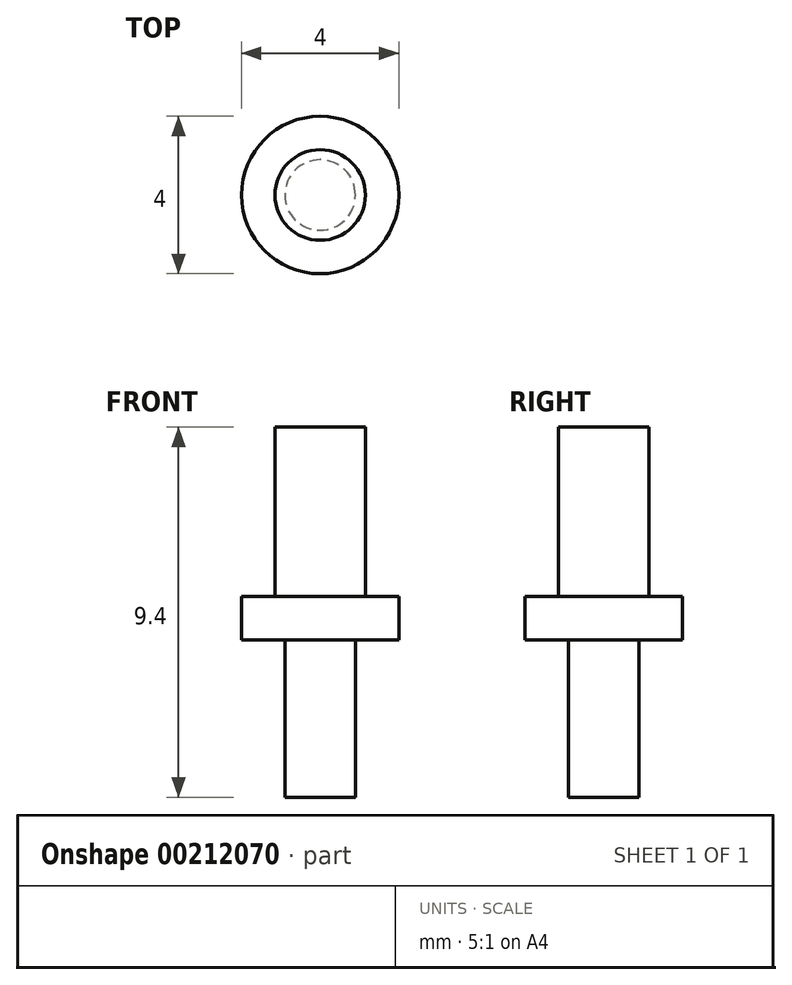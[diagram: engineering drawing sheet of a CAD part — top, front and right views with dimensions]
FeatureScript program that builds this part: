
annotation { "Feature Type Name" : "Feature", "Feature Type Description" : "" }
export const myFeature = defineFeature(function(context is Context, id is Id, definition is map)
    precondition{}
    {
        {
            var Q0;
            Q0=qCreatedBy(makeId("Top.planeOp"),FACE);
            var sketch = newSketch(context, id + "F0", { "sketchPlane" : qUnion([Q0])});
            skCircle(sketch, "E0", {"center": v(0, 0) * mm, "radius": 2 * mm});
            skSolve(sketch);
        }
        {
            var Q0;
            Q0 = qSketchRegion(id + "F0", true);
            extrude(context, id + "F1", {"entities" : qUnion([Q0]), "depth" : 1.1 * mm});
        }
        {
            var Q0;
            Q0=makeQuery(id+"F1.opExtrude","CAP_FACE",FACE,{"disambiguationData":[OSD([sQuery(id+"F0.wireOp",EDGE,"E0")])],"isStart":false});
            var sketch = newSketch(context, id + "F2", { "sketchPlane" : qUnion([Q0])});
            skCircle(sketch, "E1", {"center": v(0, 0) * mm, "radius": 1.15 * mm});
            skSolve(sketch);
        }
        {
            var Q0;
            Q0=makeQuery(id+"F2.imprint","IMPRINT",FACE,{"disambiguationData":[TD([[makeQuery(id+"F2.imprint","IMPRINT",EDGE,{"derivedFrom":sQuery(id+"F2.wireOp",EDGE,"E1")}),1.0]])]});
            extrude(context, id + "F3", {"entities" : qUnion([Q0]), "operationType" : NewBodyOperationType.ADD, "depth" : 4.3 * mm});
        }
        {
            var Q0;
            Q0=makeQuery(id+"F1.opExtrude","CAP_FACE",FACE,{"disambiguationData":[OSD([sQuery(id+"F0.wireOp",EDGE,"E0")])],"isStart":true});
            var sketch = newSketch(context, id + "F4", { "sketchPlane" : qUnion([Q0])});
            skCircle(sketch, "E2", {"center": v(0, 0) * mm, "radius": 0.9 * mm});
            skSolve(sketch);
        }
        {
            var Q0;
            Q0=makeQuery(id+"F4.imprint","IMPRINT",FACE,{"disambiguationData":[TD([[makeQuery(id+"F4.imprint","IMPRINT",EDGE,{"derivedFrom":sQuery(id+"F4.wireOp",EDGE,"E2")}),1.0]])]});
            extrude(context, id + "F5", {"entities" : qUnion([Q0]), "operationType" : NewBodyOperationType.ADD, "depth" : 4 * mm});
        }
    });
